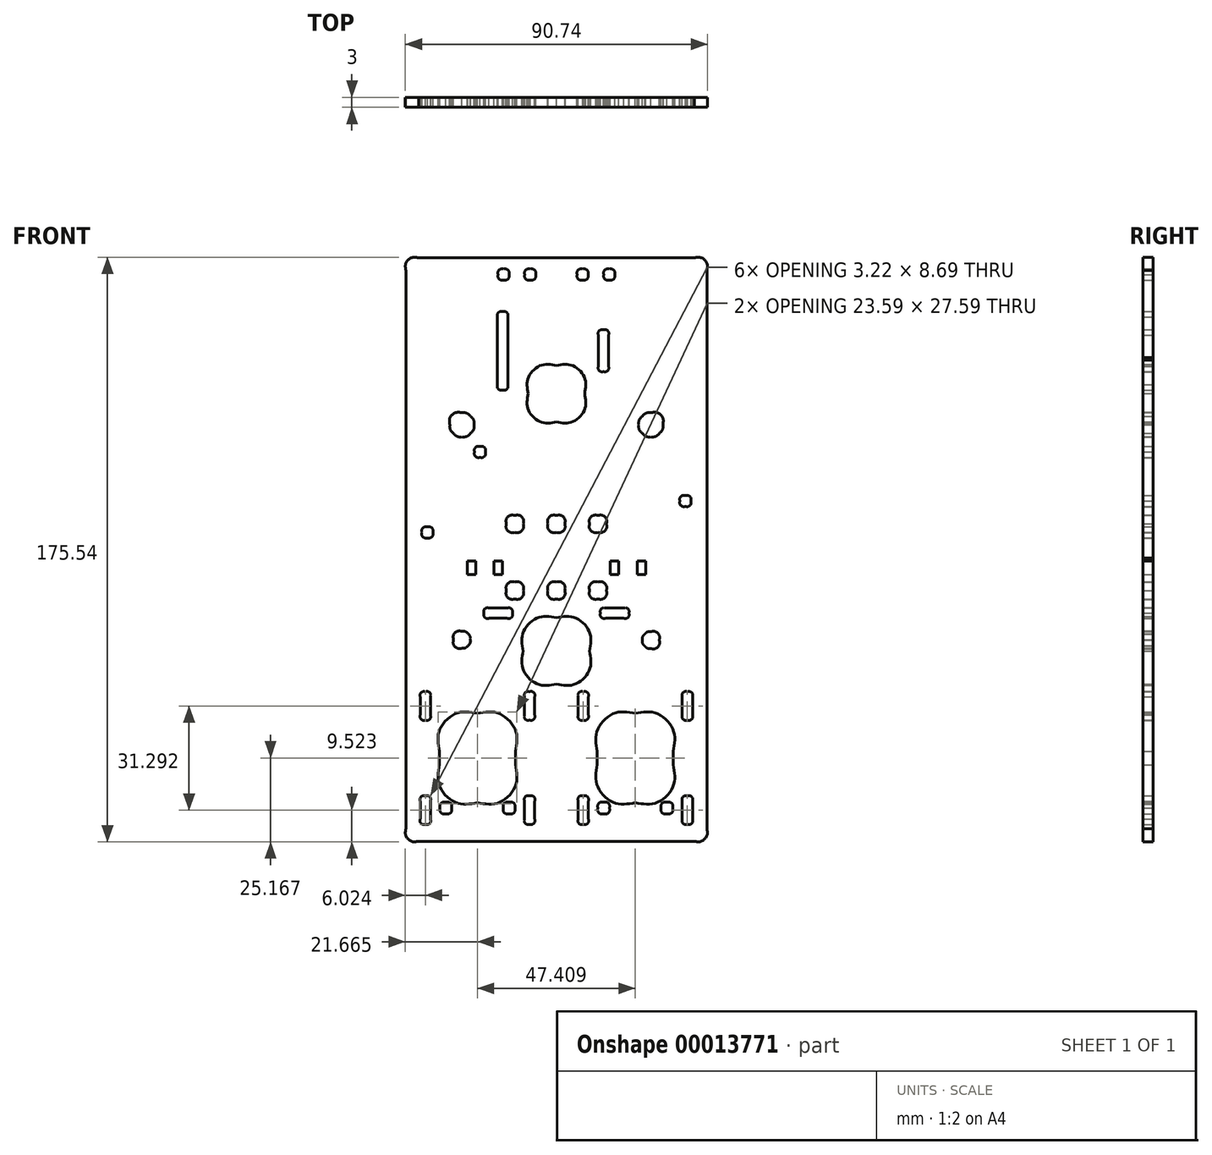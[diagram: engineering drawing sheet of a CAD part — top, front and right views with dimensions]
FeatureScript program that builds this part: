
annotation { "Feature Type Name" : "Feature", "Feature Type Description" : "" }
export const myFeature = defineFeature(function(context is Context, id is Id, definition is map)
    precondition{}
    {
        {
            var Q0;
            Q0=qCreatedBy(makeId("Front.planeOp"),FACE);
            var sketch = newSketch(context, id + "F0", { "sketchPlane" : qUnion([Q0])});
            skFitSpline(sketch, "E0", {"points": [v(-41.4, 87.62) * mm, v(-43.52, 87.62) * mm, v(-45.22, 85.92) * mm, v(-45.22, 83.8) * mm]});
            skLineSegment(sketch, "E1", {"start": v(-45.22, 83.8) * mm, "end": v(-45.22, 57.45) * mm});
            skFitSpline(sketch, "E2", {"points": [v(-45.22, 57.45) * mm, v(-45.23, 57.28) * mm, v(-45.23, 57.1) * mm, v(-45.22, 56.88) * mm]});
            skLineSegment(sketch, "E3", {"start": v(-45.22, 56.88) * mm, "end": v(-45.22, -2.6) * mm});
            skFitSpline(sketch, "E4", {"points": [v(-45.22, -2.6) * mm, v(-45.23, -2.81) * mm, v(-45.23, -3) * mm, v(-45.22, -3.16) * mm]});
            skLineSegment(sketch, "E5", {"start": v(-45.22, -3.16) * mm, "end": v(-45.22, -83.8) * mm});
            skFitSpline(sketch, "E6", {"points": [v(-45.22, -83.8) * mm, v(-45.22, -85.92) * mm, v(-43.52, -87.62) * mm, v(-41.4, -87.62) * mm]});
            skLineSegment(sketch, "E7", {"start": v(-41.4, -87.62) * mm, "end": v(-38.58, -87.62) * mm});
            skLineSegment(sketch, "E8", {"start": v(-38.58, -87.62) * mm, "end": v(-8.54, -87.62) * mm});
            skLineSegment(sketch, "E9", {"start": v(-8.54, -87.62) * mm, "end": v(8.53, -87.62) * mm});
            skLineSegment(sketch, "E10", {"start": v(8.53, -87.62) * mm, "end": v(38.58, -87.62) * mm});
            skLineSegment(sketch, "E11", {"start": v(38.58, -87.62) * mm, "end": v(41.4, -87.62) * mm});
            skFitSpline(sketch, "E12", {"points": [v(41.4, -87.62) * mm, v(43.52, -87.62) * mm, v(45.22, -85.92) * mm, v(45.22, -83.8) * mm]});
            skLineSegment(sketch, "E13", {"start": v(45.22, -83.8) * mm, "end": v(45.22, -3.41) * mm});
            skFitSpline(sketch, "E14", {"points": [v(45.22, -3.41) * mm, v(45.23, -3.18) * mm, v(45.23, -2.91) * mm, v(45.22, -2.6) * mm]});
            skLineSegment(sketch, "E15", {"start": v(45.22, -2.6) * mm, "end": v(45.22, 56.88) * mm});
            skFitSpline(sketch, "E16", {"points": [v(45.22, 56.88) * mm, v(45.23, 57.2) * mm, v(45.23, 57.46) * mm, v(45.22, 57.7) * mm]});
            skLineSegment(sketch, "E17", {"start": v(45.22, 57.7) * mm, "end": v(45.22, 83.8) * mm});
            skFitSpline(sketch, "E18", {"points": [v(45.22, 83.8) * mm, v(45.22, 85.92) * mm, v(43.52, 87.62) * mm, v(41.4, 87.62) * mm]});
            skLineSegment(sketch, "E19", {"start": v(41.4, 87.62) * mm, "end": v(38.58, 87.62) * mm});
            skLineSegment(sketch, "E20", {"start": v(38.58, 87.62) * mm, "end": v(8.53, 87.62) * mm});
            skLineSegment(sketch, "E21", {"start": v(8.53, 87.62) * mm, "end": v(-8.54, 87.62) * mm});
            skLineSegment(sketch, "E22", {"start": v(-8.54, 87.62) * mm, "end": v(-38.58, 87.62) * mm});
            skLineSegment(sketch, "E23", {"start": v(-38.58, 87.62) * mm, "end": v(-41.4, 87.62) * mm});
            skFitSpline(sketch, "E24", {"points": [v(-15.88, 84.22) * mm, v(-14.97, 84.22) * mm, v(-14.23, 83.48) * mm, v(-14.23, 82.57) * mm]});
            skFitSpline(sketch, "E25", {"points": [v(-14.23, 82.57) * mm, v(-14.23, 81.66) * mm, v(-14.97, 80.92) * mm, v(-15.88, 80.92) * mm]});
            skFitSpline(sketch, "E26", {"points": [v(-15.88, 80.92) * mm, v(-16.79, 80.92) * mm, v(-17.53, 81.66) * mm, v(-17.53, 82.57) * mm]});
            skFitSpline(sketch, "E27", {"points": [v(-17.53, 82.57) * mm, v(-17.53, 83.48) * mm, v(-16.79, 84.22) * mm, v(-15.88, 84.22) * mm]});
            skFitSpline(sketch, "E28", {"points": [v(-7.88, 84.22) * mm, v(-6.97, 84.22) * mm, v(-6.23, 83.48) * mm, v(-6.23, 82.57) * mm]});
            skFitSpline(sketch, "E29", {"points": [v(-6.23, 82.57) * mm, v(-6.23, 81.66) * mm, v(-6.97, 80.92) * mm, v(-7.88, 80.92) * mm]});
            skFitSpline(sketch, "E30", {"points": [v(-7.88, 80.92) * mm, v(-8.79, 80.92) * mm, v(-9.53, 81.66) * mm, v(-9.53, 82.57) * mm]});
            skFitSpline(sketch, "E31", {"points": [v(-9.53, 82.57) * mm, v(-9.53, 83.48) * mm, v(-8.79, 84.22) * mm, v(-7.88, 84.22) * mm]});
            skFitSpline(sketch, "E32", {"points": [v(7.88, 84.22) * mm, v(8.79, 84.22) * mm, v(9.53, 83.48) * mm, v(9.53, 82.57) * mm]});
            skFitSpline(sketch, "E33", {"points": [v(9.53, 82.57) * mm, v(9.53, 81.66) * mm, v(8.79, 80.92) * mm, v(7.88, 80.92) * mm]});
            skFitSpline(sketch, "E34", {"points": [v(7.88, 80.92) * mm, v(6.96, 80.92) * mm, v(6.23, 81.66) * mm, v(6.23, 82.57) * mm]});
            skFitSpline(sketch, "E35", {"points": [v(6.23, 82.57) * mm, v(6.23, 83.48) * mm, v(6.97, 84.22) * mm, v(7.88, 84.22) * mm]});
            skFitSpline(sketch, "E36", {"points": [v(15.88, 84.22) * mm, v(16.79, 84.22) * mm, v(17.53, 83.48) * mm, v(17.53, 82.57) * mm]});
            skFitSpline(sketch, "E37", {"points": [v(17.53, 82.57) * mm, v(17.53, 81.66) * mm, v(16.79, 80.92) * mm, v(15.88, 80.92) * mm]});
            skFitSpline(sketch, "E38", {"points": [v(15.88, 80.92) * mm, v(14.96, 80.92) * mm, v(14.23, 81.66) * mm, v(14.23, 82.57) * mm]});
            skFitSpline(sketch, "E39", {"points": [v(14.23, 82.57) * mm, v(14.23, 83.48) * mm, v(14.96, 84.22) * mm, v(15.88, 84.22) * mm]});
            skFitSpline(sketch, "E40", {"points": [v(-16.16, 71.42) * mm, v(-15.29, 71.43) * mm, v(-14.58, 70.72) * mm, v(-14.59, 69.85) * mm]});
            skLineSegment(sketch, "E41", {"start": v(-14.59, 69.85) * mm, "end": v(-14.59, 56.9) * mm});
            skLineSegment(sketch, "E42", {"start": v(-14.59, 56.9) * mm, "end": v(-14.59, 54.9) * mm});
            skLineSegment(sketch, "E43", {"start": v(-14.59, 54.9) * mm, "end": v(-14.59, 49.46) * mm});
            skFitSpline(sketch, "E44", {"points": [v(-14.59, 49.46) * mm, v(-14.57, 48.6) * mm, v(-15.27, 47.89) * mm, v(-16.14, 47.89) * mm]});
            skFitSpline(sketch, "E45", {"points": [v(-16.14, 47.89) * mm, v(-17, 47.89) * mm, v(-17.7, 48.6) * mm, v(-17.69, 49.46) * mm]});
            skLineSegment(sketch, "E46", {"start": v(-17.69, 49.46) * mm, "end": v(-17.69, 54.9) * mm});
            skLineSegment(sketch, "E47", {"start": v(-17.69, 54.9) * mm, "end": v(-17.69, 56.9) * mm});
            skLineSegment(sketch, "E48", {"start": v(-17.69, 56.9) * mm, "end": v(-17.69, 69.85) * mm});
            skFitSpline(sketch, "E49", {"points": [v(-17.69, 69.85) * mm, v(-17.7, 70.7) * mm, v(-17.02, 71.4) * mm, v(-16.16, 71.42) * mm]});
            skFitSpline(sketch, "E50", {"points": [v(14.12, 65.99) * mm, v(14.99, 66) * mm, v(15.7, 65.29) * mm, v(15.69, 64.41) * mm]});
            skLineSegment(sketch, "E51", {"start": v(15.69, 64.41) * mm, "end": v(15.69, 54.98) * mm});
            skFitSpline(sketch, "E52", {"points": [v(15.69, 54.98) * mm, v(15.7, 54.12) * mm, v(15, 53.42) * mm, v(14.14, 53.42) * mm]});
            skFitSpline(sketch, "E53", {"points": [v(14.14, 53.42) * mm, v(13.28, 53.42) * mm, v(12.58, 54.12) * mm, v(12.59, 54.98) * mm]});
            skLineSegment(sketch, "E54", {"start": v(12.59, 54.98) * mm, "end": v(12.59, 64.41) * mm});
            skFitSpline(sketch, "E55", {"points": [v(12.59, 64.41) * mm, v(12.58, 65.27) * mm, v(13.26, 65.97) * mm, v(14.12, 65.99) * mm]});
            skFitSpline(sketch, "E56", {"points": [v(0, 55.28) * mm, v(4.7, 55.28) * mm, v(8.5, 51.48) * mm, v(8.5, 46.78) * mm]});
            skFitSpline(sketch, "E57", {"points": [v(8.5, 46.78) * mm, v(8.5, 42.1) * mm, v(4.7, 38.28) * mm, v(0, 38.28) * mm]});
            skFitSpline(sketch, "E58", {"points": [v(0, 38.28) * mm, v(-4.7, 38.28) * mm, v(-8.5, 42.1) * mm, v(-8.5, 46.78) * mm]});
            skFitSpline(sketch, "E59", {"points": [v(-8.5, 46.78) * mm, v(-8.5, 51.48) * mm, v(-4.7, 55.28) * mm, v(0, 55.28) * mm]});
            skFitSpline(sketch, "E60", {"points": [v(-28.37, 41.08) * mm, v(-27.41, 41.08) * mm, v(-26.49, 40.7) * mm, v(-25.81, 40.02) * mm]});
            skFitSpline(sketch, "E61", {"points": [v(-25.81, 40.02) * mm, v(-25.13, 39.34) * mm, v(-24.75, 38.42) * mm, v(-24.75, 37.45) * mm]});
            skFitSpline(sketch, "E62", {"points": [v(-24.75, 37.45) * mm, v(-24.75, 36.5) * mm, v(-25.13, 35.57) * mm, v(-25.8, 34.9) * mm]});
            skFitSpline(sketch, "E63", {"points": [v(-25.8, 34.9) * mm, v(-26.49, 34.21) * mm, v(-27.41, 33.83) * mm, v(-28.37, 33.83) * mm]});
            skFitSpline(sketch, "E64", {"points": [v(-28.37, 33.83) * mm, v(-29.33, 33.83) * mm, v(-30.26, 34.21) * mm, v(-30.94, 34.9) * mm]});
            skFitSpline(sketch, "E65", {"points": [v(-30.94, 34.9) * mm, v(-31.62, 35.57) * mm, v(-32, 36.5) * mm, v(-32, 37.45) * mm]});
            skFitSpline(sketch, "E66", {"points": [v(-32, 37.45) * mm, v(-32, 39.46) * mm, v(-30.38, 41.08) * mm, v(-28.37, 41.08) * mm]});
            skFitSpline(sketch, "E67", {"points": [v(28.37, 41.08) * mm, v(30.37, 41.08) * mm, v(32, 39.46) * mm, v(32, 37.45) * mm]});
            skFitSpline(sketch, "E68", {"points": [v(32, 37.45) * mm, v(32, 36.5) * mm, v(31.61, 35.57) * mm, v(30.93, 34.9) * mm]});
            skFitSpline(sketch, "E69", {"points": [v(30.93, 34.9) * mm, v(30.25, 34.21) * mm, v(29.33, 33.83) * mm, v(28.37, 33.83) * mm]});
            skFitSpline(sketch, "E70", {"points": [v(28.37, 33.83) * mm, v(27.4, 33.83) * mm, v(26.48, 34.21) * mm, v(25.8, 34.9) * mm]});
            skFitSpline(sketch, "E71", {"points": [v(25.8, 34.9) * mm, v(25.13, 35.57) * mm, v(24.74, 36.5) * mm, v(24.74, 37.45) * mm]});
            skFitSpline(sketch, "E72", {"points": [v(24.74, 37.45) * mm, v(24.74, 38.42) * mm, v(25.13, 39.34) * mm, v(25.8, 40.02) * mm]});
            skFitSpline(sketch, "E73", {"points": [v(25.8, 40.02) * mm, v(26.49, 40.7) * mm, v(27.4, 41.08) * mm, v(28.37, 41.08) * mm]});
            skFitSpline(sketch, "E74", {"points": [v(-22.96, 30.95) * mm, v(-22.05, 30.95) * mm, v(-21.31, 30.21) * mm, v(-21.31, 29.3) * mm]});
            skFitSpline(sketch, "E75", {"points": [v(-21.31, 29.3) * mm, v(-21.31, 28.4) * mm, v(-22.05, 27.65) * mm, v(-22.96, 27.65) * mm]});
            skFitSpline(sketch, "E76", {"points": [v(-22.96, 27.65) * mm, v(-23.87, 27.65) * mm, v(-24.61, 28.4) * mm, v(-24.61, 29.3) * mm]});
            skFitSpline(sketch, "E77", {"points": [v(-24.61, 29.3) * mm, v(-24.61, 30.21) * mm, v(-23.87, 30.95) * mm, v(-22.96, 30.95) * mm]});
            skFitSpline(sketch, "E78", {"points": [v(38.75, 16.22) * mm, v(39.66, 16.22) * mm, v(40.4, 15.48) * mm, v(40.4, 14.57) * mm]});
            skFitSpline(sketch, "E79", {"points": [v(40.4, 14.57) * mm, v(40.4, 13.66) * mm, v(39.66, 12.92) * mm, v(38.75, 12.92) * mm]});
            skFitSpline(sketch, "E80", {"points": [v(38.75, 12.92) * mm, v(37.84, 12.92) * mm, v(37.1, 13.66) * mm, v(37.1, 14.57) * mm]});
            skFitSpline(sketch, "E81", {"points": [v(37.1, 14.57) * mm, v(37.1, 15.48) * mm, v(37.84, 16.22) * mm, v(38.75, 16.22) * mm]});
            skFitSpline(sketch, "E82", {"points": [v(-12.5, 10.25) * mm, v(-11.1, 10.25) * mm, v(-9.95, 9.1) * mm, v(-9.95, 7.7) * mm]});
            skFitSpline(sketch, "E83", {"points": [v(-9.95, 7.7) * mm, v(-9.95, 6.3) * mm, v(-11.1, 5.15) * mm, v(-12.5, 5.15) * mm]});
            skFitSpline(sketch, "E84", {"points": [v(-12.5, 5.15) * mm, v(-13.9, 5.15) * mm, v(-15.05, 6.3) * mm, v(-15.05, 7.7) * mm]});
            skFitSpline(sketch, "E85", {"points": [v(-15.05, 7.7) * mm, v(-15.05, 9.1) * mm, v(-13.9, 10.25) * mm, v(-12.5, 10.25) * mm]});
            skFitSpline(sketch, "E86", {"points": [v(0, 10.25) * mm, v(1.4, 10.25) * mm, v(2.55, 9.1) * mm, v(2.55, 7.7) * mm]});
            skFitSpline(sketch, "E87", {"points": [v(2.55, 7.7) * mm, v(2.55, 6.3) * mm, v(1.4, 5.15) * mm, v(0, 5.15) * mm]});
            skFitSpline(sketch, "E88", {"points": [v(0, 5.15) * mm, v(-1.4, 5.15) * mm, v(-2.55, 6.3) * mm, v(-2.55, 7.7) * mm]});
            skFitSpline(sketch, "E89", {"points": [v(-2.55, 7.7) * mm, v(-2.55, 9.1) * mm, v(-1.4, 10.25) * mm, v(0, 10.25) * mm]});
            skFitSpline(sketch, "E90", {"points": [v(12.5, 10.25) * mm, v(13.9, 10.25) * mm, v(15.05, 9.1) * mm, v(15.05, 7.7) * mm]});
            skFitSpline(sketch, "E91", {"points": [v(15.05, 7.7) * mm, v(15.05, 6.3) * mm, v(13.9, 5.15) * mm, v(12.5, 5.15) * mm]});
            skFitSpline(sketch, "E92", {"points": [v(12.5, 5.15) * mm, v(11.09, 5.15) * mm, v(9.95, 6.3) * mm, v(9.95, 7.7) * mm]});
            skFitSpline(sketch, "E93", {"points": [v(9.95, 7.7) * mm, v(9.95, 9.1) * mm, v(11.09, 10.25) * mm, v(12.5, 10.25) * mm]});
            skFitSpline(sketch, "E94", {"points": [v(-38.75, 6.79) * mm, v(-37.84, 6.79) * mm, v(-37.1, 6.05) * mm, v(-37.1, 5.14) * mm]});
            skFitSpline(sketch, "E95", {"points": [v(-37.1, 5.14) * mm, v(-37.1, 4.23) * mm, v(-37.84, 3.49) * mm, v(-38.75, 3.49) * mm]});
            skFitSpline(sketch, "E96", {"points": [v(-38.75, 3.49) * mm, v(-39.66, 3.49) * mm, v(-40.4, 4.23) * mm, v(-40.4, 5.14) * mm]});
            skFitSpline(sketch, "E97", {"points": [v(-40.4, 5.14) * mm, v(-40.4, 6.05) * mm, v(-39.66, 6.79) * mm, v(-38.75, 6.79) * mm]});
            skLineSegment(sketch, "E98", {"start": v(-26.78, -3.45) * mm, "end": v(-24.23, -3.45) * mm});
            skLineSegment(sketch, "E99", {"start": v(-24.23, -3.45) * mm, "end": v(-24.23, -7.55) * mm});
            skLineSegment(sketch, "E100", {"start": v(-24.23, -7.55) * mm, "end": v(-26.78, -7.55) * mm});
            skLineSegment(sketch, "E101", {"start": v(-26.78, -7.55) * mm, "end": v(-26.78, -3.45) * mm});
            skLineSegment(sketch, "E102", {"start": v(-18.74, -3.45) * mm, "end": v(-16.2, -3.45) * mm});
            skLineSegment(sketch, "E103", {"start": v(-16.2, -3.45) * mm, "end": v(-16.2, -7.55) * mm});
            skLineSegment(sketch, "E104", {"start": v(-16.2, -7.55) * mm, "end": v(-18.74, -7.55) * mm});
            skLineSegment(sketch, "E105", {"start": v(-18.74, -7.55) * mm, "end": v(-18.74, -3.45) * mm});
            skLineSegment(sketch, "E106", {"start": v(16.2, -3.45) * mm, "end": v(18.74, -3.45) * mm});
            skLineSegment(sketch, "E107", {"start": v(18.74, -3.45) * mm, "end": v(18.74, -7.55) * mm});
            skLineSegment(sketch, "E108", {"start": v(18.74, -7.55) * mm, "end": v(16.2, -7.55) * mm});
            skLineSegment(sketch, "E109", {"start": v(16.2, -7.55) * mm, "end": v(16.2, -3.45) * mm});
            skLineSegment(sketch, "E110", {"start": v(24.23, -3.45) * mm, "end": v(26.78, -3.45) * mm});
            skLineSegment(sketch, "E111", {"start": v(26.78, -3.45) * mm, "end": v(26.78, -7.55) * mm});
            skLineSegment(sketch, "E112", {"start": v(26.78, -7.55) * mm, "end": v(24.23, -7.55) * mm});
            skLineSegment(sketch, "E113", {"start": v(24.23, -7.55) * mm, "end": v(24.23, -3.45) * mm});
            skFitSpline(sketch, "E114", {"points": [v(-12.5, -9.76) * mm, v(-11.1, -9.76) * mm, v(-9.95, -10.9) * mm, v(-9.95, -12.31) * mm]});
            skFitSpline(sketch, "E115", {"points": [v(-9.95, -12.31) * mm, v(-9.95, -13.72) * mm, v(-11.1, -14.86) * mm, v(-12.5, -14.86) * mm]});
            skFitSpline(sketch, "E116", {"points": [v(-12.5, -14.86) * mm, v(-13.9, -14.86) * mm, v(-15.05, -13.72) * mm, v(-15.05, -12.31) * mm]});
            skFitSpline(sketch, "E117", {"points": [v(-15.05, -12.31) * mm, v(-15.05, -10.9) * mm, v(-13.9, -9.76) * mm, v(-12.5, -9.76) * mm]});
            skFitSpline(sketch, "E118", {"points": [v(0, -9.76) * mm, v(1.4, -9.76) * mm, v(2.55, -10.9) * mm, v(2.55, -12.31) * mm]});
            skFitSpline(sketch, "E119", {"points": [v(2.55, -12.31) * mm, v(2.55, -13.72) * mm, v(1.4, -14.86) * mm, v(0, -14.86) * mm]});
            skFitSpline(sketch, "E120", {"points": [v(0, -14.86) * mm, v(-1.4, -14.86) * mm, v(-2.55, -13.72) * mm, v(-2.55, -12.31) * mm]});
            skFitSpline(sketch, "E121", {"points": [v(-2.55, -12.31) * mm, v(-2.55, -10.9) * mm, v(-1.4, -9.76) * mm, v(0, -9.76) * mm]});
            skFitSpline(sketch, "E122", {"points": [v(12.5, -9.76) * mm, v(13.9, -9.76) * mm, v(15.05, -10.9) * mm, v(15.05, -12.31) * mm]});
            skFitSpline(sketch, "E123", {"points": [v(15.05, -12.31) * mm, v(15.05, -13.72) * mm, v(13.9, -14.86) * mm, v(12.5, -14.86) * mm]});
            skFitSpline(sketch, "E124", {"points": [v(12.5, -14.86) * mm, v(11.09, -14.86) * mm, v(9.95, -13.72) * mm, v(9.95, -12.31) * mm]});
            skFitSpline(sketch, "E125", {"points": [v(9.95, -12.31) * mm, v(9.95, -10.9) * mm, v(11.09, -9.76) * mm, v(12.5, -9.76) * mm]});
            skLineSegment(sketch, "E126", {"start": v(-20.22, -17.54) * mm, "end": v(-14.78, -17.54) * mm});
            skFitSpline(sketch, "E127", {"points": [v(-14.78, -17.54) * mm, v(-13.93, -17.53) * mm, v(-13.22, -18.22) * mm, v(-13.2, -19.07) * mm]});
            skFitSpline(sketch, "E128", {"points": [v(-13.2, -19.07) * mm, v(-13.2, -19.94) * mm, v(-13.9, -20.66) * mm, v(-14.78, -20.64) * mm]});
            skLineSegment(sketch, "E129", {"start": v(-14.78, -20.64) * mm, "end": v(-20.22, -20.64) * mm});
            skFitSpline(sketch, "E130", {"points": [v(-20.22, -20.64) * mm, v(-21.08, -20.66) * mm, v(-21.79, -19.96) * mm, v(-21.79, -19.1) * mm]});
            skFitSpline(sketch, "E131", {"points": [v(-21.79, -19.1) * mm, v(-21.79, -18.23) * mm, v(-21.08, -17.53) * mm, v(-20.22, -17.54) * mm]});
            skLineSegment(sketch, "E132", {"start": v(14.78, -17.54) * mm, "end": v(20.22, -17.54) * mm});
            skFitSpline(sketch, "E133", {"points": [v(20.22, -17.54) * mm, v(21.08, -17.53) * mm, v(21.78, -18.22) * mm, v(21.8, -19.07) * mm]});
            skFitSpline(sketch, "E134", {"points": [v(21.8, -19.07) * mm, v(21.8, -19.94) * mm, v(21.1, -20.66) * mm, v(20.22, -20.64) * mm]});
            skLineSegment(sketch, "E135", {"start": v(20.22, -20.64) * mm, "end": v(14.78, -20.64) * mm});
            skFitSpline(sketch, "E136", {"points": [v(14.78, -20.64) * mm, v(13.92, -20.66) * mm, v(13.21, -19.96) * mm, v(13.21, -19.1) * mm]});
            skFitSpline(sketch, "E137", {"points": [v(13.21, -19.1) * mm, v(13.21, -18.23) * mm, v(13.92, -17.53) * mm, v(14.78, -17.54) * mm]});
            skFitSpline(sketch, "E138", {"points": [v(0, -20.46) * mm, v(5.52, -20.46) * mm, v(10, -24.94) * mm, v(10, -30.46) * mm]});
            skFitSpline(sketch, "E139", {"points": [v(10, -30.46) * mm, v(10, -35.98) * mm, v(5.52, -40.46) * mm, v(0, -40.46) * mm]});
            skFitSpline(sketch, "E140", {"points": [v(0, -40.46) * mm, v(-5.52, -40.46) * mm, v(-10, -35.98) * mm, v(-10, -30.46) * mm]});
            skFitSpline(sketch, "E141", {"points": [v(-10, -30.46) * mm, v(-10, -24.94) * mm, v(-5.52, -20.46) * mm, v(0, -20.46) * mm]});
            skFitSpline(sketch, "E142", {"points": [v(-28.37, -24.55) * mm, v(-27.7, -24.55) * mm, v(-27.05, -24.81) * mm, v(-26.57, -25.3) * mm]});
            skFitSpline(sketch, "E143", {"points": [v(-26.57, -25.3) * mm, v(-26.1, -25.77) * mm, v(-25.82, -26.42) * mm, v(-25.82, -27.1) * mm]});
            skFitSpline(sketch, "E144", {"points": [v(-25.82, -27.1) * mm, v(-25.82, -27.77) * mm, v(-26.1, -28.42) * mm, v(-26.57, -28.9) * mm]});
            skFitSpline(sketch, "E145", {"points": [v(-26.57, -28.9) * mm, v(-27.05, -29.38) * mm, v(-27.7, -29.65) * mm, v(-28.37, -29.65) * mm]});
            skFitSpline(sketch, "E146", {"points": [v(-28.37, -29.65) * mm, v(-29.78, -29.65) * mm, v(-30.92, -28.5) * mm, v(-30.92, -27.1) * mm]});
            skFitSpline(sketch, "E147", {"points": [v(-30.92, -27.1) * mm, v(-30.92, -25.69) * mm, v(-29.78, -24.55) * mm, v(-28.37, -24.55) * mm]});
            skFitSpline(sketch, "E148", {"points": [v(28.37, -24.65) * mm, v(29.78, -24.65) * mm, v(30.92, -25.79) * mm, v(30.92, -27.2) * mm]});
            skFitSpline(sketch, "E149", {"points": [v(30.92, -27.2) * mm, v(30.92, -28.6) * mm, v(29.78, -29.75) * mm, v(28.37, -29.75) * mm]});
            skFitSpline(sketch, "E150", {"points": [v(28.37, -29.75) * mm, v(27.7, -29.75) * mm, v(27.04, -29.48) * mm, v(26.57, -29) * mm]});
            skFitSpline(sketch, "E151", {"points": [v(26.57, -29) * mm, v(26.09, -28.52) * mm, v(25.82, -27.87) * mm, v(25.82, -27.2) * mm]});
            skFitSpline(sketch, "E152", {"points": [v(25.82, -27.2) * mm, v(25.82, -26.52) * mm, v(26.09, -25.87) * mm, v(26.57, -25.4) * mm]});
            skFitSpline(sketch, "E153", {"points": [v(26.57, -25.4) * mm, v(27.04, -24.91) * mm, v(27.7, -24.65) * mm, v(28.37, -24.65) * mm]});
            skFitSpline(sketch, "E154", {"points": [v(-39.37, -42.67) * mm, v(-38.5, -42.66) * mm, v(-37.78, -43.37) * mm, v(-37.8, -44.24) * mm]});
            skLineSegment(sketch, "E155", {"start": v(-37.8, -44.24) * mm, "end": v(-37.8, -49.68) * mm});
            skFitSpline(sketch, "E156", {"points": [v(-37.8, -49.68) * mm, v(-37.78, -50.54) * mm, v(-38.48, -51.25) * mm, v(-39.35, -51.25) * mm]});
            skFitSpline(sketch, "E157", {"points": [v(-39.35, -51.25) * mm, v(-40.21, -51.25) * mm, v(-40.9, -50.54) * mm, v(-40.9, -49.68) * mm]});
            skLineSegment(sketch, "E158", {"start": v(-40.9, -49.68) * mm, "end": v(-40.9, -44.24) * mm});
            skFitSpline(sketch, "E159", {"points": [v(-40.9, -44.24) * mm, v(-40.9, -43.38) * mm, v(-40.22, -42.68) * mm, v(-39.37, -42.67) * mm]});
            skFitSpline(sketch, "E160", {"points": [v(-8.09, -42.67) * mm, v(-7.21, -42.66) * mm, v(-6.5, -43.37) * mm, v(-6.51, -44.24) * mm]});
            skLineSegment(sketch, "E161", {"start": v(-6.51, -44.24) * mm, "end": v(-6.51, -49.68) * mm});
            skFitSpline(sketch, "E162", {"points": [v(-6.51, -49.68) * mm, v(-6.5, -50.54) * mm, v(-7.2, -51.24) * mm, v(-8.06, -51.24) * mm]});
            skFitSpline(sketch, "E163", {"points": [v(-8.06, -51.24) * mm, v(-8.92, -51.24) * mm, v(-9.62, -50.54) * mm, v(-9.61, -49.68) * mm]});
            skLineSegment(sketch, "E164", {"start": v(-9.61, -49.68) * mm, "end": v(-9.61, -44.24) * mm});
            skFitSpline(sketch, "E165", {"points": [v(-9.61, -44.24) * mm, v(-9.62, -43.38) * mm, v(-8.94, -42.68) * mm, v(-8.09, -42.67) * mm]});
            skFitSpline(sketch, "E166", {"points": [v(8.09, -42.67) * mm, v(8.94, -42.68) * mm, v(9.63, -43.38) * mm, v(9.61, -44.24) * mm]});
            skLineSegment(sketch, "E167", {"start": v(9.61, -44.24) * mm, "end": v(9.61, -49.68) * mm});
            skFitSpline(sketch, "E168", {"points": [v(9.61, -49.68) * mm, v(9.63, -50.54) * mm, v(8.93, -51.25) * mm, v(8.06, -51.25) * mm]});
            skFitSpline(sketch, "E169", {"points": [v(8.06, -51.25) * mm, v(7.2, -51.25) * mm, v(6.5, -50.54) * mm, v(6.51, -49.68) * mm]});
            skLineSegment(sketch, "E170", {"start": v(6.51, -49.68) * mm, "end": v(6.51, -44.24) * mm});
            skFitSpline(sketch, "E171", {"points": [v(6.51, -44.24) * mm, v(6.5, -43.37) * mm, v(7.21, -42.66) * mm, v(8.09, -42.67) * mm]});
            skFitSpline(sketch, "E172", {"points": [v(39.37, -42.67) * mm, v(40.22, -42.68) * mm, v(40.9, -43.38) * mm, v(40.9, -44.24) * mm]});
            skLineSegment(sketch, "E173", {"start": v(40.9, -44.24) * mm, "end": v(40.9, -49.68) * mm});
            skFitSpline(sketch, "E174", {"points": [v(40.9, -49.68) * mm, v(40.9, -50.54) * mm, v(40.21, -51.25) * mm, v(39.35, -51.25) * mm]});
            skFitSpline(sketch, "E175", {"points": [v(39.35, -51.25) * mm, v(38.48, -51.25) * mm, v(37.78, -50.54) * mm, v(37.8, -49.68) * mm]});
            skLineSegment(sketch, "E176", {"start": v(37.8, -49.68) * mm, "end": v(37.8, -44.24) * mm});
            skFitSpline(sketch, "E177", {"points": [v(37.8, -44.24) * mm, v(37.78, -43.37) * mm, v(38.5, -42.66) * mm, v(39.37, -42.67) * mm]});
            skFitSpline(sketch, "E178", {"points": [v(-23.7, -49.18) * mm, v(-17.4, -49.18) * mm, v(-12.28, -54.3) * mm, v(-12.28, -60.6) * mm]});
            skLineSegment(sketch, "E179", {"start": v(-12.28, -60.6) * mm, "end": v(-12.28, -64.6) * mm});
            skFitSpline(sketch, "E180", {"points": [v(-12.28, -64.6) * mm, v(-12.28, -70.91) * mm, v(-17.4, -76.03) * mm, v(-23.7, -76.03) * mm]});
            skFitSpline(sketch, "E181", {"points": [v(-23.7, -76.03) * mm, v(-30.01, -76.03) * mm, v(-35.13, -70.91) * mm, v(-35.13, -64.6) * mm]});
            skLineSegment(sketch, "E182", {"start": v(-35.13, -64.6) * mm, "end": v(-35.13, -60.6) * mm});
            skFitSpline(sketch, "E183", {"points": [v(-35.13, -60.6) * mm, v(-35.13, -54.3) * mm, v(-30.01, -49.18) * mm, v(-23.7, -49.18) * mm]});
            skFitSpline(sketch, "E184", {"points": [v(23.7, -49.18) * mm, v(30.01, -49.18) * mm, v(35.13, -54.3) * mm, v(35.13, -60.6) * mm]});
            skLineSegment(sketch, "E185", {"start": v(35.13, -60.6) * mm, "end": v(35.13, -64.6) * mm});
            skFitSpline(sketch, "E186", {"points": [v(35.13, -64.6) * mm, v(35.13, -70.91) * mm, v(30.01, -76.03) * mm, v(23.7, -76.03) * mm]});
            skFitSpline(sketch, "E187", {"points": [v(23.7, -76.03) * mm, v(17.4, -76.03) * mm, v(12.28, -70.91) * mm, v(12.28, -64.6) * mm]});
            skLineSegment(sketch, "E188", {"start": v(12.28, -64.6) * mm, "end": v(12.28, -60.6) * mm});
            skFitSpline(sketch, "E189", {"points": [v(12.28, -60.6) * mm, v(12.28, -54.3) * mm, v(17.4, -49.18) * mm, v(23.7, -49.18) * mm]});
            skFitSpline(sketch, "E190", {"points": [v(-39.37, -73.96) * mm, v(-38.5, -73.95) * mm, v(-37.78, -74.66) * mm, v(-37.8, -75.53) * mm]});
            skLineSegment(sketch, "E191", {"start": v(-37.8, -75.53) * mm, "end": v(-37.8, -80.97) * mm});
            skFitSpline(sketch, "E192", {"points": [v(-37.8, -80.97) * mm, v(-37.78, -81.83) * mm, v(-38.48, -82.54) * mm, v(-39.35, -82.54) * mm]});
            skFitSpline(sketch, "E193", {"points": [v(-39.35, -82.54) * mm, v(-40.21, -82.54) * mm, v(-40.9, -81.83) * mm, v(-40.9, -80.97) * mm]});
            skLineSegment(sketch, "E194", {"start": v(-40.9, -80.97) * mm, "end": v(-40.9, -75.53) * mm});
            skFitSpline(sketch, "E195", {"points": [v(-40.9, -75.53) * mm, v(-40.9, -74.68) * mm, v(-40.22, -73.97) * mm, v(-39.37, -73.96) * mm]});
            skFitSpline(sketch, "E196", {"points": [v(-8.09, -73.96) * mm, v(-7.21, -73.95) * mm, v(-6.5, -74.66) * mm, v(-6.51, -75.53) * mm]});
            skLineSegment(sketch, "E197", {"start": v(-6.51, -75.53) * mm, "end": v(-6.51, -80.97) * mm});
            skFitSpline(sketch, "E198", {"points": [v(-6.51, -80.97) * mm, v(-6.5, -81.83) * mm, v(-7.2, -82.53) * mm, v(-8.06, -82.53) * mm]});
            skFitSpline(sketch, "E199", {"points": [v(-8.06, -82.53) * mm, v(-8.92, -82.53) * mm, v(-9.62, -81.83) * mm, v(-9.61, -80.97) * mm]});
            skLineSegment(sketch, "E200", {"start": v(-9.61, -80.97) * mm, "end": v(-9.61, -75.53) * mm});
            skFitSpline(sketch, "E201", {"points": [v(-9.61, -75.53) * mm, v(-9.62, -74.68) * mm, v(-8.94, -73.97) * mm, v(-8.09, -73.96) * mm]});
            skFitSpline(sketch, "E202", {"points": [v(8.09, -73.96) * mm, v(8.94, -73.97) * mm, v(9.63, -74.68) * mm, v(9.61, -75.53) * mm]});
            skLineSegment(sketch, "E203", {"start": v(9.61, -75.53) * mm, "end": v(9.61, -80.97) * mm});
            skFitSpline(sketch, "E204", {"points": [v(9.61, -80.97) * mm, v(9.63, -81.83) * mm, v(8.93, -82.54) * mm, v(8.06, -82.54) * mm]});
            skFitSpline(sketch, "E205", {"points": [v(8.06, -82.54) * mm, v(7.2, -82.54) * mm, v(6.5, -81.83) * mm, v(6.51, -80.97) * mm]});
            skLineSegment(sketch, "E206", {"start": v(6.51, -80.97) * mm, "end": v(6.51, -75.53) * mm});
            skFitSpline(sketch, "E207", {"points": [v(6.51, -75.53) * mm, v(6.5, -74.66) * mm, v(7.21, -73.95) * mm, v(8.09, -73.96) * mm]});
            skFitSpline(sketch, "E208", {"points": [v(39.37, -73.96) * mm, v(40.22, -73.97) * mm, v(40.9, -74.68) * mm, v(40.9, -75.53) * mm]});
            skLineSegment(sketch, "E209", {"start": v(40.9, -75.53) * mm, "end": v(40.9, -80.97) * mm});
            skFitSpline(sketch, "E210", {"points": [v(40.9, -80.97) * mm, v(40.9, -81.83) * mm, v(40.21, -82.54) * mm, v(39.35, -82.54) * mm]});
            skFitSpline(sketch, "E211", {"points": [v(39.35, -82.54) * mm, v(38.48, -82.54) * mm, v(37.78, -81.83) * mm, v(37.8, -80.97) * mm]});
            skLineSegment(sketch, "E212", {"start": v(37.8, -80.97) * mm, "end": v(37.8, -75.53) * mm});
            skFitSpline(sketch, "E213", {"points": [v(37.8, -75.53) * mm, v(37.78, -74.66) * mm, v(38.5, -73.95) * mm, v(39.37, -73.96) * mm]});
            skFitSpline(sketch, "E214", {"points": [v(-33.2, -75.87) * mm, v(-32.24, -75.87) * mm, v(-31.45, -76.65) * mm, v(-31.45, -77.62) * mm]});
            skFitSpline(sketch, "E215", {"points": [v(-31.45, -77.62) * mm, v(-31.45, -78.59) * mm, v(-32.24, -79.37) * mm, v(-33.2, -79.37) * mm]});
            skFitSpline(sketch, "E216", {"points": [v(-33.2, -79.37) * mm, v(-34.17, -79.37) * mm, v(-34.95, -78.59) * mm, v(-34.95, -77.62) * mm]});
            skFitSpline(sketch, "E217", {"points": [v(-34.95, -77.62) * mm, v(-34.95, -76.65) * mm, v(-34.17, -75.87) * mm, v(-33.2, -75.87) * mm]});
            skFitSpline(sketch, "E218", {"points": [v(-14.2, -75.87) * mm, v(-13.24, -75.87) * mm, v(-12.46, -76.65) * mm, v(-12.46, -77.62) * mm]});
            skFitSpline(sketch, "E219", {"points": [v(-12.46, -77.62) * mm, v(-12.46, -78.59) * mm, v(-13.24, -79.37) * mm, v(-14.2, -79.37) * mm]});
            skFitSpline(sketch, "E220", {"points": [v(-14.2, -79.37) * mm, v(-15.17, -79.37) * mm, v(-15.96, -78.59) * mm, v(-15.96, -77.62) * mm]});
            skFitSpline(sketch, "E221", {"points": [v(-15.96, -77.62) * mm, v(-15.96, -76.65) * mm, v(-15.17, -75.87) * mm, v(-14.2, -75.87) * mm]});
            skFitSpline(sketch, "E222", {"points": [v(14.2, -75.87) * mm, v(15.17, -75.87) * mm, v(15.95, -76.65) * mm, v(15.95, -77.62) * mm]});
            skFitSpline(sketch, "E223", {"points": [v(15.95, -77.62) * mm, v(15.95, -78.59) * mm, v(15.17, -79.37) * mm, v(14.2, -79.37) * mm]});
            skFitSpline(sketch, "E224", {"points": [v(14.2, -79.37) * mm, v(13.24, -79.37) * mm, v(12.45, -78.59) * mm, v(12.45, -77.62) * mm]});
            skFitSpline(sketch, "E225", {"points": [v(12.45, -77.62) * mm, v(12.45, -76.65) * mm, v(13.24, -75.87) * mm, v(14.2, -75.87) * mm]});
            skFitSpline(sketch, "E226", {"points": [v(33.2, -75.87) * mm, v(34.17, -75.87) * mm, v(34.95, -76.65) * mm, v(34.95, -77.62) * mm]});
            skFitSpline(sketch, "E227", {"points": [v(34.95, -77.62) * mm, v(34.95, -78.59) * mm, v(34.17, -79.37) * mm, v(33.2, -79.37) * mm]});
            skFitSpline(sketch, "E228", {"points": [v(33.2, -79.37) * mm, v(32.24, -79.37) * mm, v(31.45, -78.59) * mm, v(31.45, -77.62) * mm]});
            skFitSpline(sketch, "E229", {"points": [v(31.45, -77.62) * mm, v(31.45, -76.65) * mm, v(32.24, -75.87) * mm, v(33.2, -75.87) * mm]});
            skSolve(sketch);
        }
        {
            var Q0;
            Q0 = qSketchRegion(id + "F0", true);
            extrude(context, id + "F1", {"entities" : qUnion([Q0]), "depth" : 3 * mm});
        }
    });
